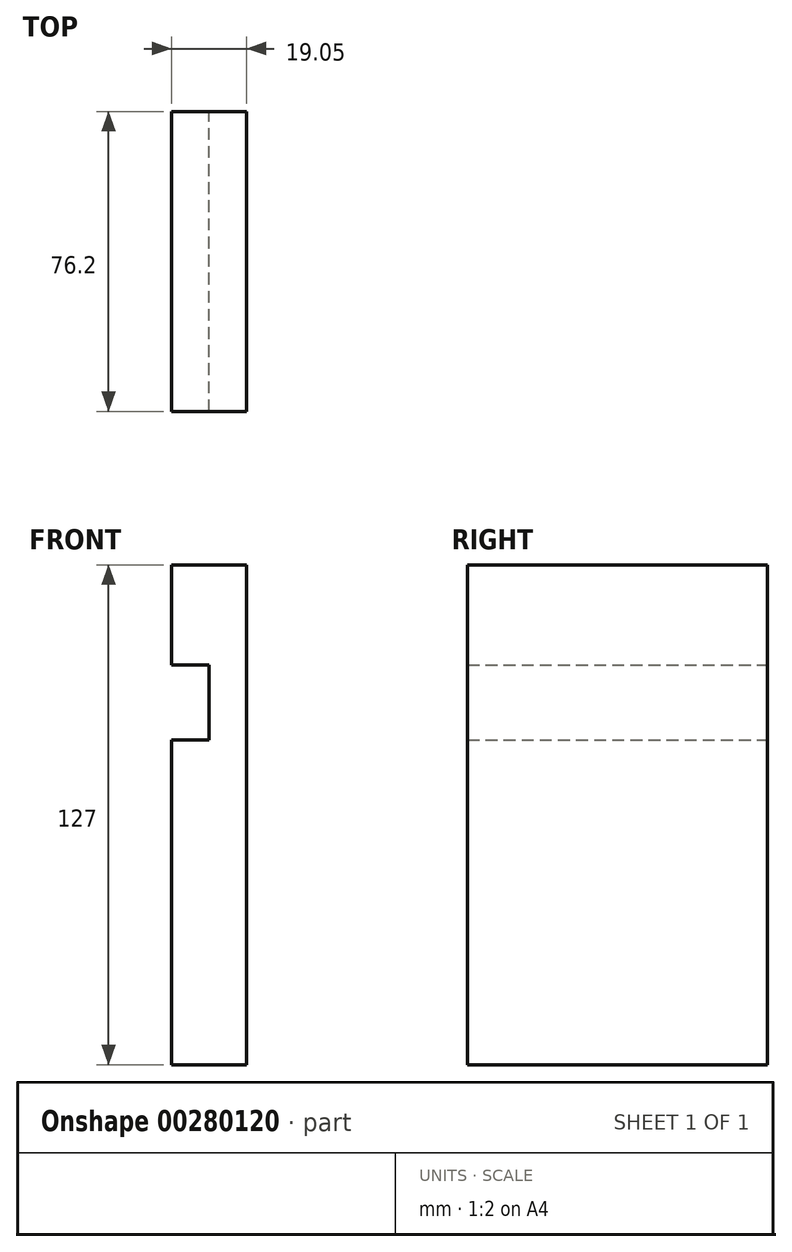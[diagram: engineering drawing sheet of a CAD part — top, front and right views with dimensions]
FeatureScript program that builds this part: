
annotation { "Feature Type Name" : "Feature", "Feature Type Description" : "" }
export const myFeature = defineFeature(function(context is Context, id is Id, definition is map)
    precondition{}
    {
        {
            var Q0;
            Q0=qCreatedBy(makeId("Front.planeOp"),FACE);
            var sketch = newSketch(context, id + "F0", { "sketchPlane" : qUnion([Q0])});
            skLineSegment(sketch, "E0", {"start": v(-18, 72.76) * mm, "end": v(-18, -54.24) * mm});
            skLineSegment(sketch, "E1", {"start": v(-18, 72.76) * mm, "end": v(-37.05, 72.76) * mm});
            skLineSegment(sketch, "E2", {"start": v(-37.05, 72.76) * mm, "end": v(-37.05, 47.36) * mm});
            skLineSegment(sketch, "E3", {"start": v(-37.05, 47.36) * mm, "end": v(-27.52, 47.36) * mm});
            skLineSegment(sketch, "E4", {"start": v(-27.52, 47.36) * mm, "end": v(-27.52, 28.3) * mm});
            skLineSegment(sketch, "E5", {"start": v(-27.52, 28.3) * mm, "end": v(-37.05, 28.3) * mm});
            skLineSegment(sketch, "E6", {"start": v(-37.05, 28.3) * mm, "end": v(-37.05, -54.24) * mm});
            skLineSegment(sketch, "E7", {"start": v(-37.05, -54.24) * mm, "end": v(-18, -54.24) * mm});
            skSolve(sketch);
        }
        {
            var Q0;
            Q0 = qSketchRegion(id + "F0", true);
            extrude(context, id + "F1", {"entities" : qUnion([Q0]), "depth" : 76.2 * mm});
        }
    });
